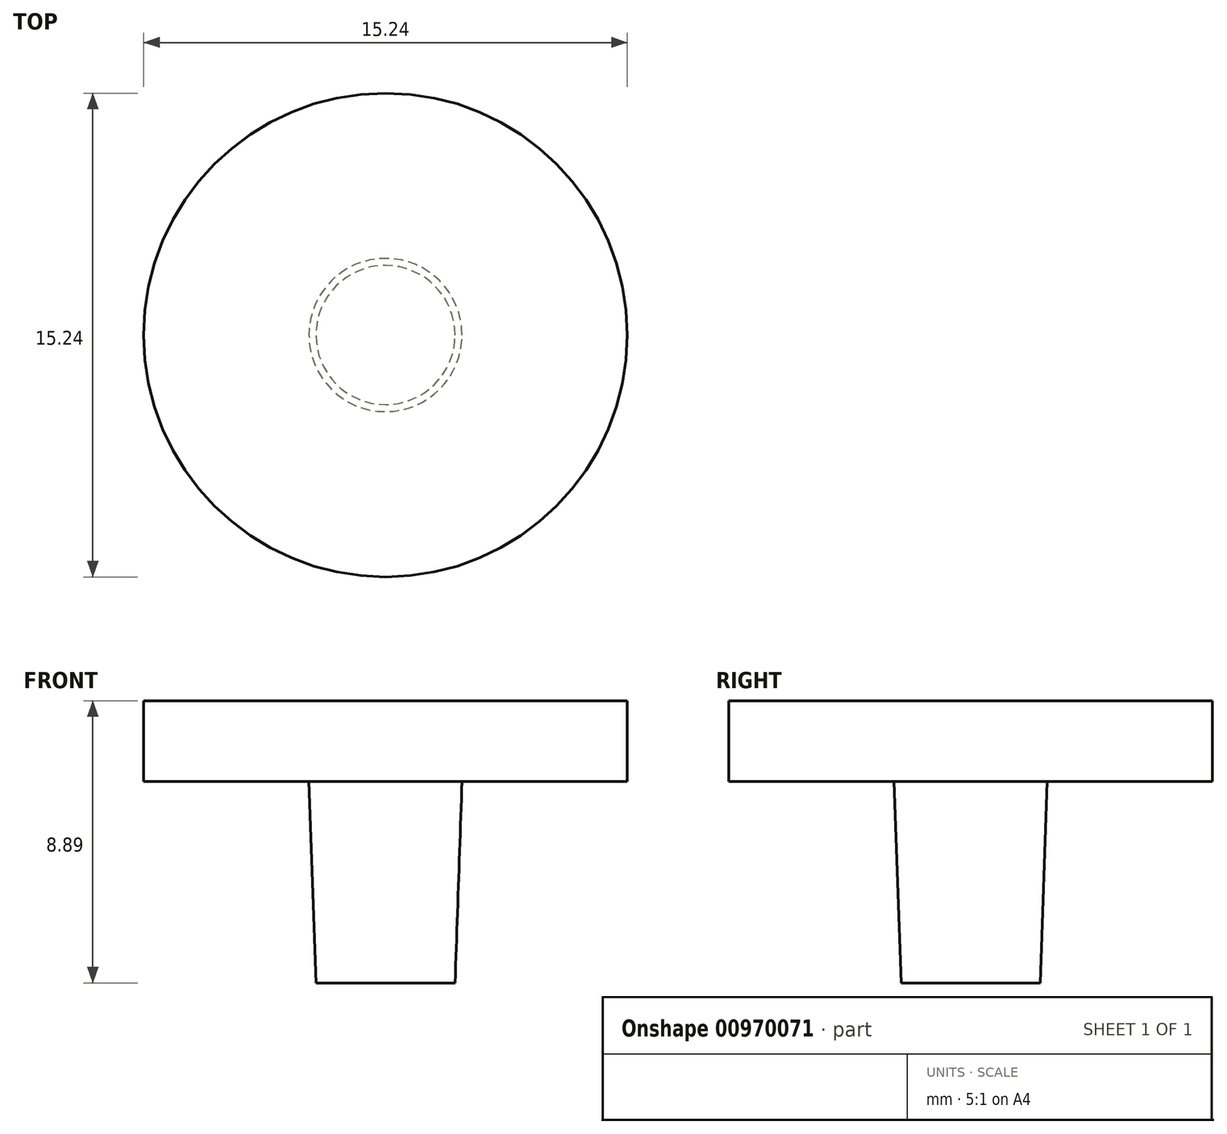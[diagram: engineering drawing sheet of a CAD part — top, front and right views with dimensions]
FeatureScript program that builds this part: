
annotation { "Feature Type Name" : "Feature", "Feature Type Description" : "" }
export const myFeature = defineFeature(function(context is Context, id is Id, definition is map)
    precondition{}
    {
        {
            var Q0;
            Q0=qCreatedBy(makeId("Top.planeOp"),FACE);
            var sketch = newSketch(context, id + "F0", { "sketchPlane" : qUnion([Q0])});
            skCircle(sketch, "E0", {"center": v(0, 0) * mm, "radius": 7.62 * mm});
            skSolve(sketch);
        }
        {
            var Q0;
            Q0=makeQuery(id+"F0.imprint","IMPRINT",FACE,{"disambiguationData":[TD([[makeQuery(id+"F0.imprint","IMPRINT",EDGE,{"derivedFrom":sQuery(id+"F0.wireOp",EDGE,"E0")}),1.0]])]});
            extrude(context, id + "F1", {"entities" : qUnion([Q0]), "depth" : 2.54 * mm, "offsetDistance" : 25.4 * mm});
        }
        {
            var Q0;
            Q0=qCreatedBy(makeId("Top.planeOp"),FACE);
            var sketch = newSketch(context, id + "F2", { "sketchPlane" : qUnion([Q0])});
            skCircle(sketch, "E1", {"center": v(0, 0) * mm, "radius": 2.41 * mm});
            skSolve(sketch);
        }
        {
            var Q0;
            Q0=qSketchRegion(id+"F2",true);
            var Q1;
            Q1=sQuery(id+"F2.wireOp",EDGE,"E1");
            extrude(context, id + "F3", {"entities" : qUnion([Q0]), "operationType" : NewBodyOperationType.ADD, "surfaceEntities" : qUnion([Q1]), "oppositeDirection" : true, "depth" : 6.35 * mm, "offsetDistance" : 25.4 * mm, "hasDraft" : true, "draftAngle" : 2 * degree, "draftPullDirection" : true});
        }
    });
